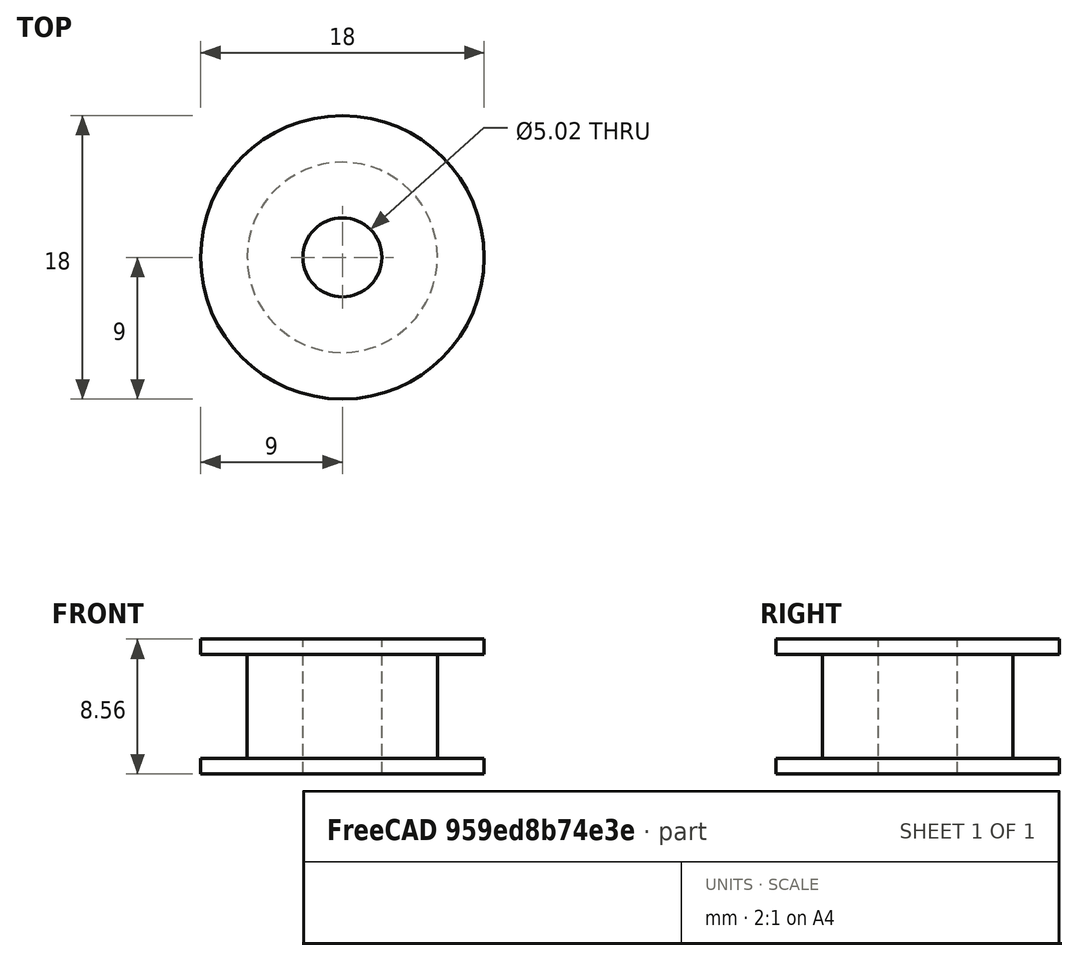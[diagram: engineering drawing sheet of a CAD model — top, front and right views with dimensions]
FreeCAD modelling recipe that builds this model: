
FCSTD DOCUMENT  (FreeCAD 0.20R29177 +426 (Git))
Label: SmoothIdlerPulleyGT2
License: All rights reserved
LicenseURL: http://en.wikipedia.org/wiki/All_rights_reserved
objects: App::DocumentObjectGroup×3, PartDesign::CoordinateSystem×1, App::FeaturePython×1, Sketcher::SketchObject×1, PartDesign::Revolution×1, PartDesign::Body×1, App::Part×1
note: 5 computed .brp shape members not serialized (recipe doc carries the construction recipe); baked Part::Feature solids carry a one-line shape summary decoded from their .brp

FEATURE [App::DocumentObjectGroup] Parts
FEATURE [PartDesign::CoordinateSystem] LCS_Origin
  AttacherType = Attacher::AttachEngine3D
  MapMode = 2
  Support = -> [X_Axis]
FEATURE [App::FeaturePython] Variables  # WARN: FeaturePython — macro-defined, semantics opaque (R4)
  Type = App::PropertyContainer
FEATURE [App::DocumentObjectGroup] Constraints
FEATURE [App::DocumentObjectGroup] Configurations
FEATURE [Sketcher::SketchObject] Sketch
  FullyConstrained = true
  MapMode = 5
  Placement = pos=(0,0,0) rot=(1,0,0;1.5708rad)
  Support = -> [XZ_Plane001]
  sketch-geometry (8):
    g0: LineSegment StartX=2.51 StartY=0 StartZ=0 EndX=2.51 EndY=8.56 EndZ=0
    g1: LineSegment StartX=2.51 StartY=8.56 StartZ=0 EndX=9 EndY=8.56 EndZ=0
    g2: LineSegment StartX=9 StartY=8.56 StartZ=0 EndX=9 EndY=7.58 EndZ=0
    g3: LineSegment StartX=9 StartY=7.58 StartZ=0 EndX=6.045 EndY=7.58 EndZ=0
    g4: LineSegment StartX=6.045 StartY=7.58 StartZ=0 EndX=6.045 EndY=0.98 EndZ=0
    g5: LineSegment StartX=6.045 StartY=0.98 StartZ=0 EndX=9 EndY=0.98 EndZ=0
    g6: LineSegment StartX=9 StartY=0.98 StartZ=0 EndX=9 EndY=0 EndZ=0
    g7: LineSegment StartX=9 StartY=0 StartZ=0 EndX=2.51 EndY=0 EndZ=0
  constraints (24):
    c: PointOnObject(g0,g-1)
    c: Vertical(g0)
    c: Coincident(g0,g1)
    c: Horizontal(g1)
    c: Coincident(g1,g2)
    c: Coincident(g2,g3)
    c: Horizontal(g3)
    c: Coincident(g3,g4)
    c: Vertical(g4)
    c: Coincident(g4,g5)
    c: Horizontal(g5)
    c: Coincident(g5,g6)
    c: PointOnObject(g6,g-1)
    c: Vertical(g6)
    c: Coincident(g6,g7)
    c: Coincident(g7,g0)
    c: Vertical(g2)
    c: DistanceX(g-1,g3) = 6.045
    c: DistanceX(g-1,g0) = 2.51
    c: DistanceY(g4,g4) = 6.6
    c: PointOnObject(g2,g6)
    c: DistanceX(g-1,g6) = 9
    c: DistanceY(g-1,g0) = 8.56
    c: Equal(g2,g6)
FEATURE [PartDesign::Revolution] Revolution
  Angle = 360
  Axis = (0,-2e-16,1)
  Base = (0,0,0)
  Placement = pos=(0,0,0) rot=(1,0,0;1.5708rad)
  Profile = -> Sketch
  ReferenceAxis = -> Sketch [V_Axis]
  Reversed = true
FEATURE [PartDesign::Body] Body
  Group = -> [Sketch,Revolution]
  Origin = -> Origin001
  Tip = -> Revolution
FEATURE [App::Part] Assembly
  AssemblyType = Part::Link
  Group = -> [LCS_Origin,Variables,Constraints,Configurations,Body]
  Origin = -> Origin
  Type = Assembly
